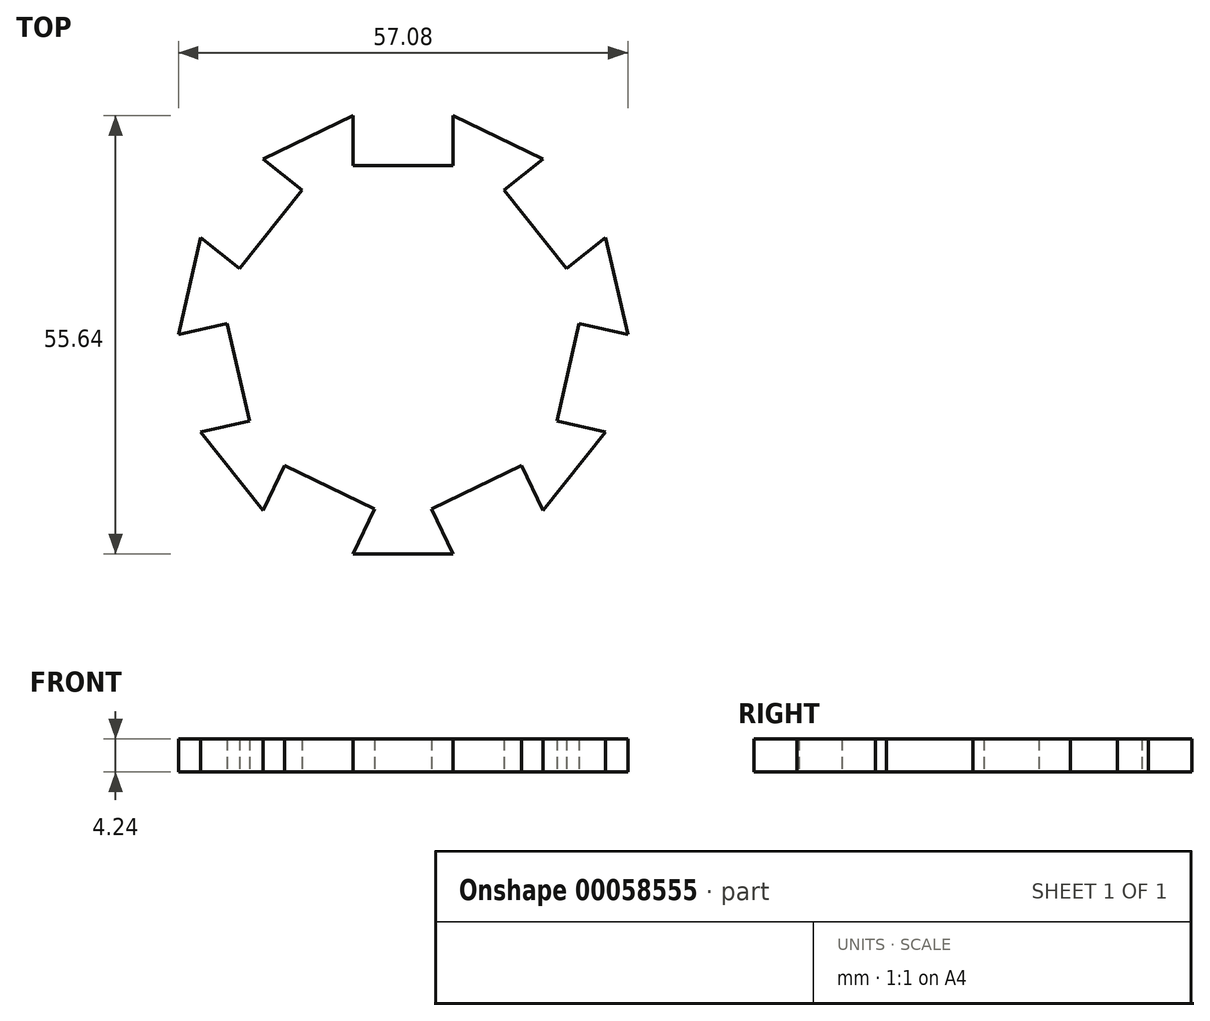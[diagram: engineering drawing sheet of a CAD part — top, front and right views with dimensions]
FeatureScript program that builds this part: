
annotation { "Feature Type Name" : "Feature", "Feature Type Description" : "" }
export const myFeature = defineFeature(function(context is Context, id is Id, definition is map)
    precondition{}
    {
        {
            var Q0;
            Q0=qCreatedBy(makeId("Top.planeOp"),FACE);
            var sketch = newSketch(context, id + "F0", { "sketchPlane" : qUnion([Q0])});
            skCircle(sketch, "E0.cCircle", {"center": v(0, 0) * mm, "radius": 27.82 * mm, "construction": true});
            skLineSegment(sketch, "E0.0", {"start": v(-6.35, 27.82) * mm, "end": v(6.35, 27.82) * mm});
            skLineSegment(sketch, "E0.1", {"start": v(6.35, 27.82) * mm, "end": v(17.8, 22.31) * mm});
            skLineSegment(sketch, "E0.2", {"start": v(17.8, 22.31) * mm, "end": v(25.71, 12.38) * mm});
            skLineSegment(sketch, "E0.3", {"start": v(25.71, 12.38) * mm, "end": v(28.54, 0) * mm});
            skLineSegment(sketch, "E0.4", {"start": v(28.54, 0) * mm, "end": v(25.71, -12.38) * mm});
            skLineSegment(sketch, "E0.5", {"start": v(25.71, -12.38) * mm, "end": v(17.8, -22.31) * mm});
            skLineSegment(sketch, "E0.6", {"start": v(17.8, -22.31) * mm, "end": v(6.35, -27.82) * mm});
            skLineSegment(sketch, "E0.7", {"start": v(6.35, -27.82) * mm, "end": v(-6.35, -27.82) * mm});
            skLineSegment(sketch, "E0.8", {"start": v(-6.35, -27.82) * mm, "end": v(-17.8, -22.31) * mm});
            skLineSegment(sketch, "E0.9", {"start": v(-17.8, -22.31) * mm, "end": v(-25.71, -12.38) * mm});
            skLineSegment(sketch, "E0.10", {"start": v(-25.71, -12.38) * mm, "end": v(-28.54, 0) * mm});
            skLineSegment(sketch, "E0.11", {"start": v(-28.54, 0) * mm, "end": v(-25.71, 12.38) * mm});
            skLineSegment(sketch, "E0.12", {"start": v(-25.71, 12.38) * mm, "end": v(-17.8, 22.31) * mm});
            skLineSegment(sketch, "E0.13", {"start": v(-17.8, 22.31) * mm, "end": v(-6.35, 27.82) * mm});
            skPoint(sketch, "E0.0.midPoint", {"position": v(0, 27.82) * mm});
            skLineSegment(sketch, "E1.rect.bottom", {"start": v(-6.35, 34.17) * mm, "end": v(6.35, 34.17) * mm});
            skLineSegment(sketch, "E1.rect.top", {"start": v(-6.35, 21.47) * mm, "end": v(6.35, 21.47) * mm});
            skLineSegment(sketch, "E1.rect.left", {"start": v(-6.35, 34.17) * mm, "end": v(-6.35, 21.47) * mm});
            skLineSegment(sketch, "E1.rect.right", {"start": v(6.35, 34.17) * mm, "end": v(6.35, 21.47) * mm});
            skLineSegment(sketch, "E2", {"start": v(-22.76, 26.27) * mm, "end": v(-12.83, 18.35) * mm});
            skLineSegment(sketch, "E3", {"start": v(-12.83, 18.35) * mm, "end": v(-20.75, 8.42) * mm});
            skLineSegment(sketch, "E4", {"start": v(-20.75, 8.42) * mm, "end": v(-30.68, 16.34) * mm});
            skLineSegment(sketch, "E5", {"start": v(-30.68, 16.34) * mm, "end": v(-22.76, 26.27) * mm});
            skLineSegment(sketch, "E6", {"start": v(-34.73, -1.41) * mm, "end": v(-22.35, 1.41) * mm});
            skLineSegment(sketch, "E7", {"start": v(-31.9, -13.8) * mm, "end": v(-34.73, -1.41) * mm});
            skLineSegment(sketch, "E8", {"start": v(-19.52, -10.97) * mm, "end": v(-31.9, -13.8) * mm});
            skLineSegment(sketch, "E9", {"start": v(-19.52, -10.97) * mm, "end": v(-22.35, 1.41) * mm});
            skLineSegment(sketch, "E10", {"start": v(-15.04, -16.59) * mm, "end": v(-20.55, -28.03) * mm});
            skLineSegment(sketch, "E11", {"start": v(-20.55, -28.03) * mm, "end": v(-9.1, -33.54) * mm});
            skLineSegment(sketch, "E12", {"start": v(-9.1, -33.54) * mm, "end": v(-3.6, -22.1) * mm});
            skLineSegment(sketch, "E13", {"start": v(-3.6, -22.1) * mm, "end": v(-15.04, -16.59) * mm});
            skLineSegment(sketch, "E14.MirrorCS", {"start": v(12.83, 18.35) * mm, "end": v(20.75, 8.42) * mm});
            skLineSegment(sketch, "E15.MirrorCS", {"start": v(22.76, 26.27) * mm, "end": v(12.83, 18.35) * mm});
            skLineSegment(sketch, "E16.MirrorCS", {"start": v(30.68, 16.34) * mm, "end": v(22.76, 26.27) * mm});
            skLineSegment(sketch, "E17.MirrorCS", {"start": v(20.75, 8.42) * mm, "end": v(30.68, 16.34) * mm});
            skLineSegment(sketch, "E18.MirrorCS", {"start": v(34.73, -1.41) * mm, "end": v(22.35, 1.41) * mm});
            skLineSegment(sketch, "E19.MirrorCS", {"start": v(19.52, -10.97) * mm, "end": v(22.35, 1.41) * mm});
            skLineSegment(sketch, "E20.MirrorCS", {"start": v(31.9, -13.8) * mm, "end": v(34.73, -1.41) * mm});
            skLineSegment(sketch, "E21.MirrorCS", {"start": v(19.52, -10.97) * mm, "end": v(31.9, -13.8) * mm});
            skLineSegment(sketch, "E22.MirrorCS", {"start": v(3.6, -22.1) * mm, "end": v(15.04, -16.59) * mm});
            skLineSegment(sketch, "E23.MirrorCS", {"start": v(20.55, -28.03) * mm, "end": v(9.1, -33.54) * mm});
            skLineSegment(sketch, "E24.MirrorCS", {"start": v(15.04, -16.59) * mm, "end": v(20.55, -28.03) * mm});
            skLineSegment(sketch, "E25.MirrorCS", {"start": v(9.1, -33.54) * mm, "end": v(3.6, -22.1) * mm});
            skSolve(sketch);
        }
        {
            var Q0;
            {var subQ2=sQuery(id+"F0.wireOp",EDGE,"E0.1");Q0=makeQuery(id+"F0.imprint","IMPRINT",FACE,{"disambiguationData":[TD([[makeQuery(id+"F0.imprint","IMPRINT",EDGE,{"derivedFrom":subQ2}),-1.0]])]});}
            extrude(context, id + "F1", {"entities" : qUnion([Q0]), "depth" : 4.23 * mm, "symmetric" : true});
        }
    });
